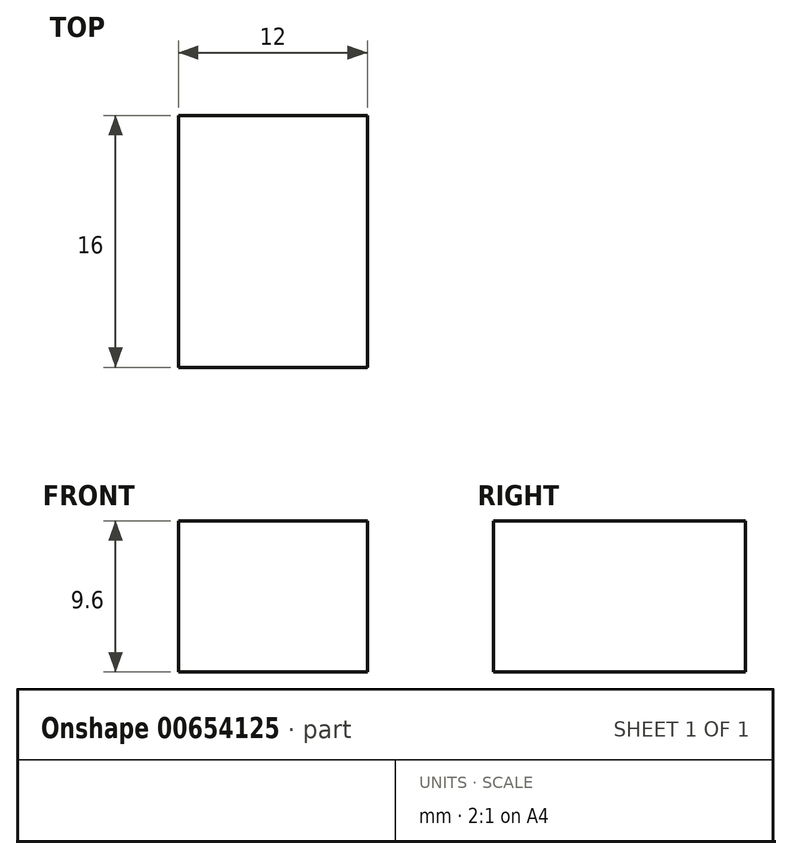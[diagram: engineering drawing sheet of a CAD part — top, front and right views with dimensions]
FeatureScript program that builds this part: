
annotation { "Feature Type Name" : "Feature", "Feature Type Description" : "" }
export const myFeature = defineFeature(function(context is Context, id is Id, definition is map)
    precondition{}
    {
        {
            var Q0;
            Q0=qCreatedBy(makeId("Top.planeOp"),FACE);
            var sketch = newSketch(context, id + "F0", { "sketchPlane" : qUnion([Q0])});
            skLineSegment(sketch, "E0.bottom", {"start": v(0, 0) * mm, "end": v(-12, 0) * mm});
            skLineSegment(sketch, "E0.top", {"start": v(0, 16) * mm, "end": v(-12, 16) * mm});
            skLineSegment(sketch, "E0.left", {"start": v(0, 0) * mm, "end": v(0, 16) * mm});
            skLineSegment(sketch, "E0.right", {"start": v(-12, 0) * mm, "end": v(-12, 16) * mm});
            skSolve(sketch);
        }
        {
            var Q0;
            Q0=makeQuery(id+"F0.imprint","IMPRINT",FACE,{"disambiguationData":[TD([[makeQuery(id+"F0.imprint","IMPRINT",EDGE,{"derivedFrom":sQuery(id+"F0.wireOp",EDGE,"E0.bottom")}),-1.0]])]});
            extrude(context, id + "F1", {"entities" : qUnion([Q0]), "depth" : 9.6 * mm, "offsetDistance" : 25.4 * mm});
        }
    });
